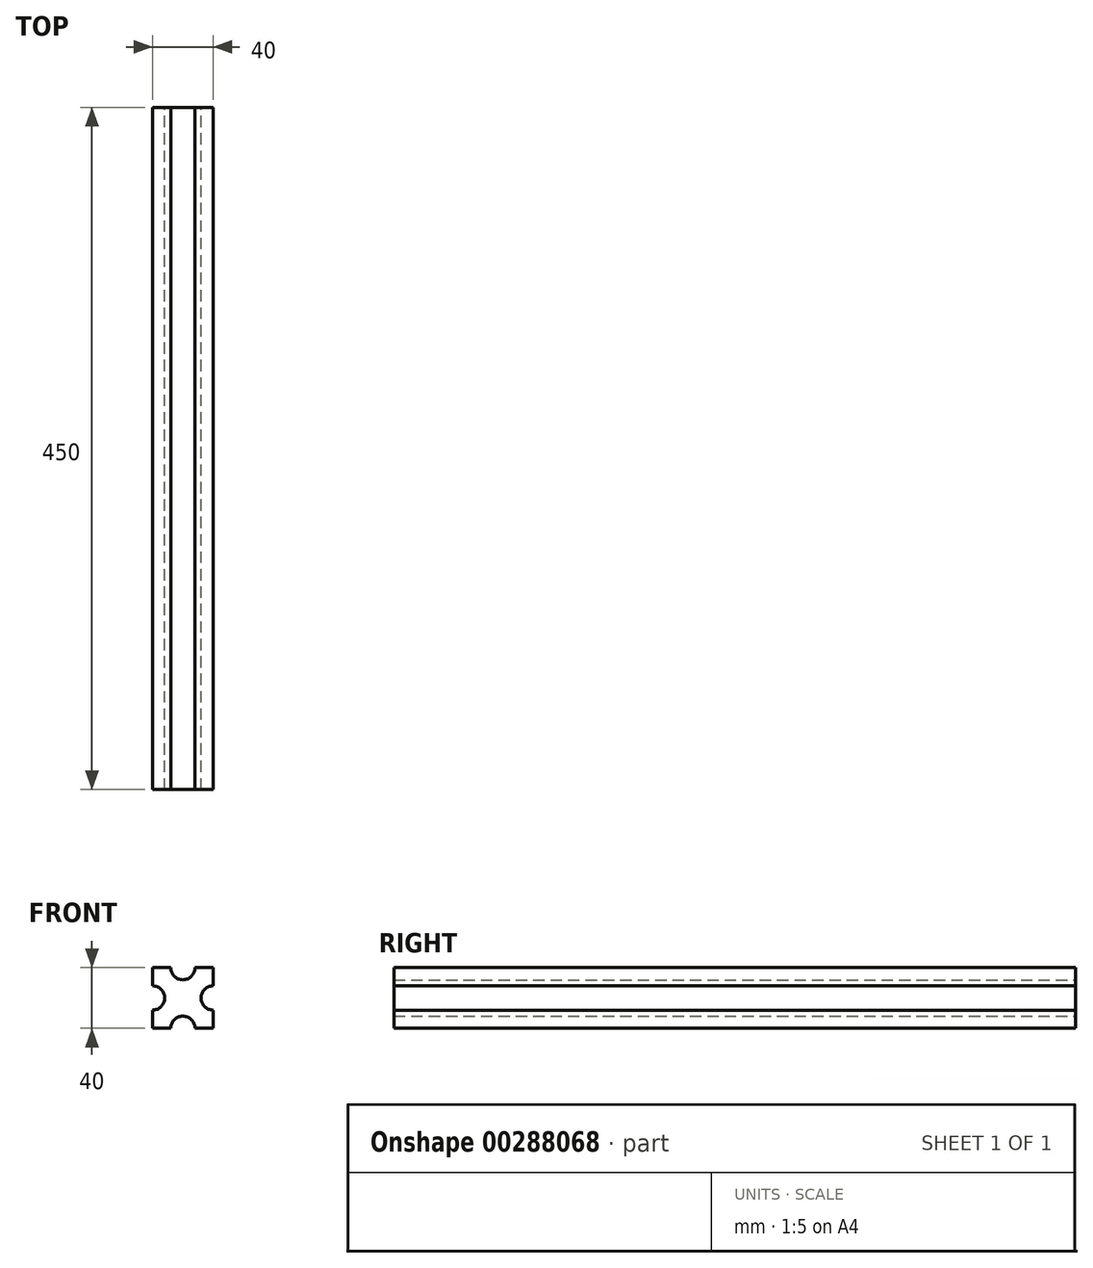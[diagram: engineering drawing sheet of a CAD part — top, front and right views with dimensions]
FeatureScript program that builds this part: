
annotation { "Feature Type Name" : "Feature", "Feature Type Description" : "" }
export const myFeature = defineFeature(function(context is Context, id is Id, definition is map)
    precondition{}
    {
        {
            var Q0;
            Q0=qCreatedBy(makeId("Front.planeOp"),FACE);
            var sketch = newSketch(context, id + "F0", { "sketchPlane" : qUnion([Q0])});
            skLineSegment(sketch, "E0.bottom", {"start": v(20, -20) * mm, "end": v(-20, -20) * mm});
            skLineSegment(sketch, "E0.top", {"start": v(20, 20) * mm, "end": v(-20, 20) * mm});
            skLineSegment(sketch, "E0.left", {"start": v(20, -20) * mm, "end": v(20, 20) * mm});
            skLineSegment(sketch, "E0.right", {"start": v(-20, -20) * mm, "end": v(-20, 20) * mm});
            skPoint(sketch, "E0.middle", {"position": v(0, 0) * mm});
            skCircle(sketch, "E1", {"center": v(0, 20) * mm, "radius": 8 * mm});
            skCircle(sketch, "E2", {"center": v(-20, 0) * mm, "radius": 8 * mm});
            skCircle(sketch, "E3", {"center": v(0, -20) * mm, "radius": 8 * mm});
            skCircle(sketch, "E4", {"center": v(20, 0) * mm, "radius": 8 * mm});
            skSolve(sketch);
        }
        {
            var Q0;
            {var subQ4=sQuery(id+"F0.wireOp",EDGE,"E0.bottom");var subQ6=sQuery(id+"F0.wireOp",EDGE,"E0.left");var subQ11=makeQuery(id+"F0.imprint","INTERSECT",VERTEX,{"derivedFrom":[subQ4,subQ6]});Q0=makeQuery(id+"F0.imprint","IMPRINT",FACE,{"disambiguationData":[TD([[makeQuery(id+"F0.imprint","IMPRINT",EDGE,{"disambiguationData":[TD([[subQ11,-1.0]])],"derivedFrom":subQ4}),-1.0]])]});}
            extrude(context, id + "F1", {"entities" : qUnion([Q0]), "depth" : 450 * mm});
        }
    });
